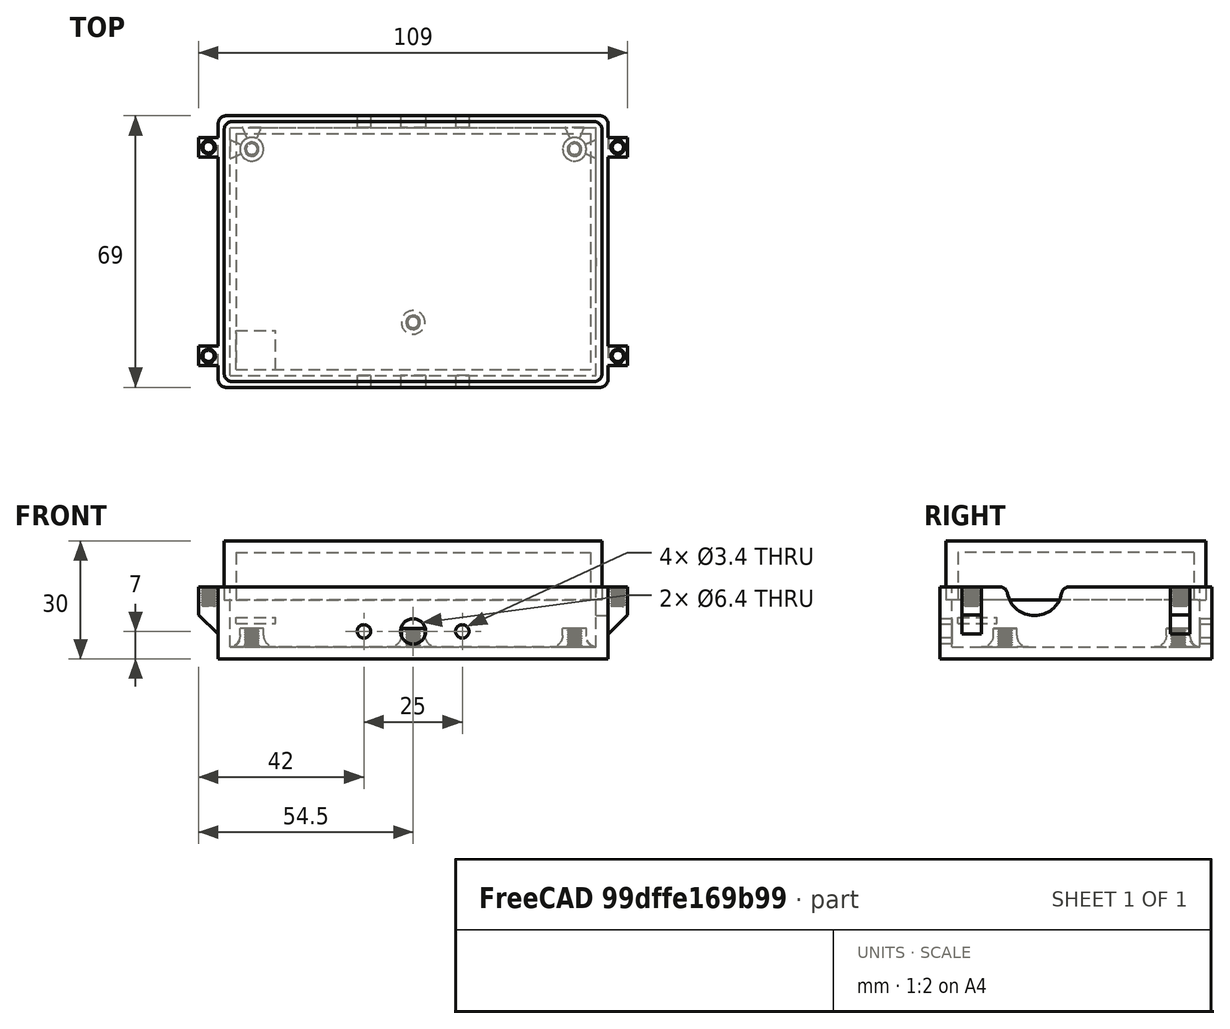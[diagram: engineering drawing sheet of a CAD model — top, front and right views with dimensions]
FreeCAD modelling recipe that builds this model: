
FCSTD DOCUMENT  (FreeCAD 0.18.4R)
Label: PCB_Case
License: All rights reserved
LicenseURL: http://en.wikipedia.org/wiki/All_rights_reserved
objects: Part::Cylinder×10, Part::Box×7, Part::FeaturePython×7, Part::Cut×7, Part::MultiFuse×5, Part::Chamfer×4, Part::Fillet×4, Part::Thickness×2
note: 46 computed .brp shape members not serialized (recipe doc carries the construction recipe); baked Part::Feature solids carry a one-line shape summary decoded from their .brp

FEATURE [Part::Box] Box  label="Cube"
  AttacherType = Attacher::AttachEngine3D
  Height = 15.3
  Length = 93
  Placement = pos=(-1.5,-1.5,0) rot=(0,0,1;0rad)
  Width = 63
FEATURE [Part::Cylinder] Cylinder
  Angle = 360
  AttacherType = Attacher::AttachEngine3D
  Height = 4.8
  Placement = pos=(86,56,0) rot=(0,0,1;0rad)
  Radius = 3
FEATURE [Part::Cylinder] Cylinder001
  Angle = 360
  AttacherType = Attacher::AttachEngine3D
  Height = 4.8
  Placement = pos=(4,56,0) rot=(0,0,1;0rad)
  Radius = 3
FEATURE [Part::Cylinder] Cylinder002
  Angle = 360
  AttacherType = Attacher::AttachEngine3D
  Height = 4.8
  Placement = pos=(45,12,0) rot=(0,0,1;0rad)
  Radius = 3
FEATURE [Part::Thickness] Thickness
  Faces = -> Box [Face6]
  Intersection = false
  Join = 2
  Mode = 0
  SelfIntersection = false
  Value = 3
FEATURE [Part::Cylinder] Cylinder003
  Angle = 360
  AttacherType = Attacher::AttachEngine3D
  Height = 10
  Placement = pos=(32.5,4,4) rot=(1,0,0;1.5708rad)
  Radius = 1.7
FEATURE [Part::Cylinder] Cylinder004
  Angle = 360
  AttacherType = Attacher::AttachEngine3D
  Height = 10
  Placement = pos=(57.5,4,4) rot=(1,0,0;1.5708rad)
  Radius = 1.7
FEATURE [Part::Cylinder] Cylinder007
  Angle = 360
  AttacherType = Attacher::AttachEngine3D
  Height = 10
  Placement = pos=(45,4,4) rot=(1,0,0;1.5708rad)
  Radius = 3.2
FEATURE [Part::Cylinder] Cylinder008
  Angle = 360
  AttacherType = Attacher::AttachEngine3D
  Height = 10
  Placement = pos=(57.5,67,4) rot=(1,0,0;1.5708rad)
  Radius = 1.7
FEATURE [Part::Cylinder] Cylinder010
  Angle = 360
  AttacherType = Attacher::AttachEngine3D
  Height = 10
  Placement = pos=(45,67,4) rot=(1,0,0;1.5708rad)
  Radius = 3.2
FEATURE [Part::Cylinder] Cylinder011
  Angle = 360
  AttacherType = Attacher::AttachEngine3D
  Height = 10
  Placement = pos=(32.5,67,4) rot=(1,0,0;1.5708rad)
  Radius = 1.7
FEATURE [Part::Box] Box001  label="Cube001"
  AttacherType = Attacher::AttachEngine3D
  Height = 12
  Length = 5
  Placement = pos=(-9,0,0) rot=(0,0,1;0rad)
  Width = 5
FEATURE [Part::Chamfer] Chamfer
  Base = -> Box001
  Edges = 1 edges r=4.9: [Edge4]
  Placement = pos=(1,1,0) rot=(0,0,1;0rad)
FEATURE [Part::FeaturePython] ScrewTap  label="(M3.5)x20.0-ScrewTap"  # Fasteners workbench fastener (typed FeaturePython)
  Placement = pos=(-5.5,3.5,27.5) rot=(0,0,1;0rad)
  diameter = 5
  invert = false
  length = 20
  matchOuter = false
  offset = 0
  thread = true
FEATURE [Part::Cut] Cut
  Base = -> Chamfer
  Placement = pos=(-1.5,0,3.3) rot=(0,0,1;0rad)
  Tool = -> ScrewTap
FEATURE [Part::Box] Box002  label="Cube002"
  AttacherType = Attacher::AttachEngine3D
  Height = 12
  Length = 5
  Placement = pos=(-9,0,0) rot=(0,0,1;0rad)
  Width = 5
FEATURE [Part::Chamfer] Chamfer001
  Base = -> Box002
  Edges = 1 edges r=4.9: [Edge4]
  Placement = pos=(1,1,0) rot=(0,0,1;0rad)
FEATURE [Part::FeaturePython] ScrewTap001  label="(M3.5)x20.0-ScrewTap001"  # Fasteners workbench fastener (typed FeaturePython)
  Placement = pos=(-5.5,3.5,27.5) rot=(0,0,1;0rad)
  diameter = 5
  invert = false
  length = 20
  matchOuter = false
  offset = 0
  thread = true
FEATURE [Part::Cut] Cut001
  Base = -> Chamfer001
  Placement = pos=(-1.5,53,3.3) rot=(0,0,1;0rad)
  Tool = -> ScrewTap001
FEATURE [Part::Box] Box003  label="Cube003"
  AttacherType = Attacher::AttachEngine3D
  Height = 12
  Length = 5
  Placement = pos=(-9,0,0) rot=(0,0,1;0rad)
  Width = 5
FEATURE [Part::Chamfer] Chamfer002
  Base = -> Box003
  Edges = 1 edges r=4.9: [Edge4]
  Placement = pos=(1,1,0) rot=(0,0,1;0rad)
FEATURE [Part::FeaturePython] ScrewTap002  label="(M3.5)x20.0-ScrewTap002"  # Fasteners workbench fastener (typed FeaturePython)
  Placement = pos=(-5.5,3.5,27.5) rot=(0,0,1;0rad)
  diameter = 5
  invert = false
  length = 20
  matchOuter = false
  offset = 0
  thread = true
FEATURE [Part::Cut] Cut002
  Base = -> Chamfer002
  Placement = pos=(91.5,60,3.3) rot=(0,0,1;3.14159rad)
  Tool = -> ScrewTap002
FEATURE [Part::FeaturePython] ScrewTap003  label="(M3.5)x20.0-ScrewTap003"  # Fasteners workbench fastener (typed FeaturePython)
  Placement = pos=(-5.5,3.5,27.5) rot=(0,0,1;0rad)
  diameter = 5
  invert = false
  length = 20
  matchOuter = false
  offset = 0
  thread = true
FEATURE [Part::Box] Box004  label="Cube004"
  AttacherType = Attacher::AttachEngine3D
  Height = 12
  Length = 5
  Placement = pos=(-9,0,0) rot=(0,0,1;0rad)
  Width = 5
FEATURE [Part::Chamfer] Chamfer003
  Base = -> Box004
  Edges = 1 edges r=4.9: [Edge4]
  Placement = pos=(1,1,0) rot=(0,0,1;0rad)
FEATURE [Part::Cut] Cut003
  Base = -> Chamfer003
  Placement = pos=(91.5,7,3.3) rot=(0,0,1;3.14159rad)
  Tool = -> ScrewTap003
FEATURE [Part::Fillet] Fillet
  Base = -> Thickness
  Edges = 4 edges r=2: [Edge17,Edge19,Edge20,Edge22]
FEATURE [Part::Box] Box005  label="Cube005"
  AttacherType = Attacher::AttachEngine3D
  Height = 12
  Length = 90
  Width = 60
FEATURE [Part::Thickness] Thickness001
  Faces = -> Box005 [Face6]
  Intersection = false
  Join = 2
  Mode = 0
  SelfIntersection = false
  Value = 3
FEATURE [Part::Fillet] Fillet001
  Base = -> Thickness001
  Edges = 4 edges r=2: [Edge17,Edge19,Edge20,Edge22]
  Placement = pos=(0,60,24) rot=(1,0,0;3.14159rad)
FEATURE [Part::MultiFuse] Fusion
  Shapes = -> [Fillet,Cut003,Cut002,Cut001,Cut]
FEATURE [Part::MultiFuse] Fusion001
  Shapes = -> [Cylinder011,Cylinder010,Cylinder008,Cylinder007,Cylinder004,Cylinder003]
FEATURE [Part::Cut] Cut004
  Base = -> Fusion
  Tool = -> Fusion001
FEATURE [Part::FeaturePython] ScrewTap004  label="(M3.5)x7.0-ScrewTap"  # Fasteners workbench fastener (typed FeaturePython)
  Placement = pos=(45,12,7) rot=(0,0,1;0rad)
  diameter = 5
  invert = false
  length = 7
  matchOuter = false
  offset = 0
  thread = true
FEATURE [Part::FeaturePython] ScrewTap005  label="(M3.5)x7.0-ScrewTap001"  # Fasteners workbench fastener (typed FeaturePython)
  Placement = pos=(4,56,7) rot=(0,0,1;0rad)
  diameter = 5
  invert = false
  length = 7
  matchOuter = false
  offset = 0
  thread = true
FEATURE [Part::FeaturePython] ScrewTap006  label="(M3.5)x7.0-ScrewTap002"  # Fasteners workbench fastener (typed FeaturePython)
  Placement = pos=(86,56,7) rot=(0,0,1;0rad)
  diameter = 5
  invert = false
  length = 7
  matchOuter = false
  offset = 0
  thread = true
FEATURE [Part::MultiFuse] Fusion002
  Shapes = -> [ScrewTap004,ScrewTap005,ScrewTap006]
FEATURE [Part::MultiFuse] Fusion003
  Shapes = -> [Cylinder,Cylinder001,Cylinder002]
FEATURE [Part::Cut] Cut005
  Base = -> Fusion003
  Tool = -> Fusion002
FEATURE [Part::MultiFuse] Fusion004
  Shapes = -> [Cut004,Cut005]
FEATURE [Part::Box] Box006  label="Cube006"
  AttacherType = Attacher::AttachEngine3D
  Height = 1.6
  Length = 10
  Placement = pos=(0,0,6) rot=(0,0,1;0rad)
  Width = 10
FEATURE [Part::Fillet] Fillet002
  Base = -> Fusion004
  Edges = 3 edges r=3: [Edge179,Edge180,Edge181]
FEATURE [Part::Cylinder] Cylinder012
  Angle = 360
  AttacherType = Attacher::AttachEngine3D
  Height = 10
  Placement = pos=(87,19.5,15) rot=(0,1,0;1.5708rad)
  Radius = 7
FEATURE [Part::Cut] Cut006
  Base = -> Fillet002
  Tool = -> Cylinder012
FEATURE [Part::Fillet] Fillet003
  Base = -> Cut006
  Edges = 2 edges r=2: [Edge35,Edge39]
